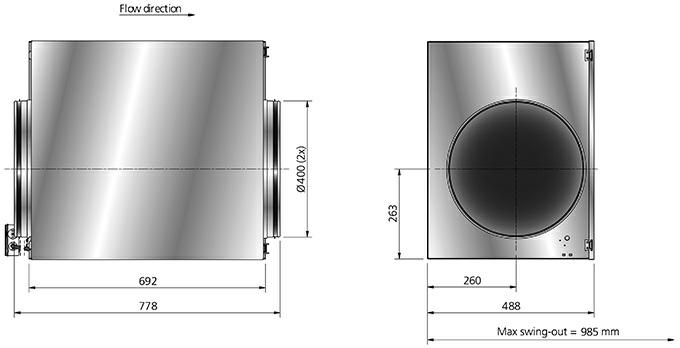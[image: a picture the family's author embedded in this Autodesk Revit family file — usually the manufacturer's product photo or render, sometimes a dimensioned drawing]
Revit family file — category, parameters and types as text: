
# Revit family: IRE 630 E3 ErP AC_
name_source: partatom
category: Mechanical Equipment
revit_build: Autodesk Revit MEP 2014 (Build: 20130308_1515(x64)
units: mm (PartAtom-declared; Revit-internal decimal feet)

## types (1)
- IRE 630 E3 ErP AC
    Capacitor = - μF
    Current = 9 A
    Depth = 955 mm  [stored 3.1332 ft]
    Description = Insulated duct fans with circular connections
    Diameter = 630 mm  [stored 2.06693 ft]
    Frequency = 50 Hz
    Height = 703 mm  [stored 2.30643 ft]
    Main Material = Steel, Galvanized
    Max. temperature of transported air = 55 °C
    Max. temperature of transported air when speed controlled = 55 °C
    Phase = 3
    Power = 3210 W
    Sound pressure level at 3 m = 56 dB(A)
    Speed = 1390 rpm
    Voltage = 400 V
    Voltage range = 380-415 V
    Weight = 113.00 kg
    Width = 1067 mm  [stored 3.50066 ft]
    Wiring diagram = Y 4040004 / Δ 4040003

note: [stored X ft] marks values corroborated as IEEE doubles in the binary element streams (Revit-internal decimal feet)

## geometry (parser evidence)
native form markers: Sweep x5
no freeform markers — native parametric forms only
